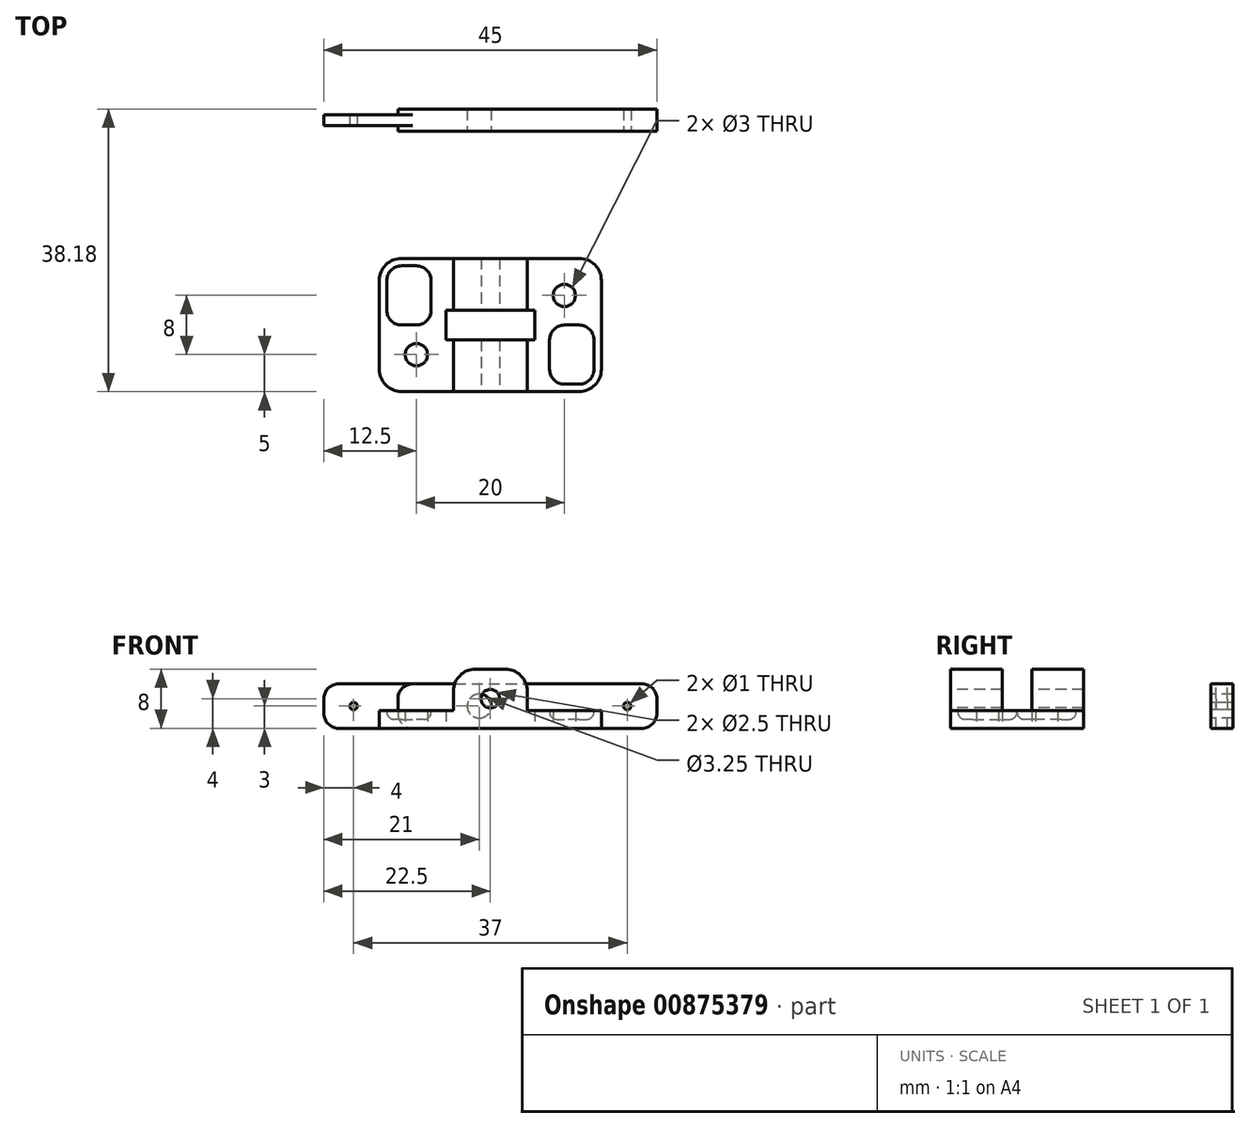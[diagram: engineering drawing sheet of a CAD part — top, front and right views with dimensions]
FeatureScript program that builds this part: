
annotation { "Feature Type Name" : "Feature", "Feature Type Description" : "" }
export const myFeature = defineFeature(function(context is Context, id is Id, definition is map)
    precondition{}
    {
        {
            var Q0;
            Q0=qCreatedBy(makeId("Top.planeOp"),FACE);
            var sketch = newSketch(context, id + "F0", { "sketchPlane" : qUnion([Q0])});
            skLineSegment(sketch, "E0.bottom", {"start": v(15, 9) * mm, "end": v(-15, 9) * mm});
            skLineSegment(sketch, "E0.top", {"start": v(15, -9) * mm, "end": v(-15, -9) * mm});
            skLineSegment(sketch, "E0.left", {"start": v(15, 9) * mm, "end": v(15, -9) * mm});
            skLineSegment(sketch, "E0.right", {"start": v(-15, 9) * mm, "end": v(-15, -9) * mm});
            skPoint(sketch, "E0.middle", {"position": v(0, 0) * mm});
            skLineSegment(sketch, "E1.bottom", {"start": v(6, 2) * mm, "end": v(-6, 2) * mm});
            skLineSegment(sketch, "E1.top", {"start": v(6, -2) * mm, "end": v(-6, -2) * mm});
            skLineSegment(sketch, "E1.left", {"start": v(6, 2) * mm, "end": v(6, -2) * mm});
            skLineSegment(sketch, "E1.right", {"start": v(-6, 2) * mm, "end": v(-6, -2) * mm});
            skLineSegment(sketch, "E2.bottom", {"start": v(15, 9) * mm, "end": v(10, 9) * mm, "construction": true});
            skLineSegment(sketch, "E2.top", {"start": v(15, 4) * mm, "end": v(10, 4) * mm, "construction": true});
            skLineSegment(sketch, "E2.left", {"start": v(15, 9) * mm, "end": v(15, 4) * mm, "construction": true});
            skLineSegment(sketch, "E2.right", {"start": v(10, 9) * mm, "end": v(10, 4) * mm, "construction": true});
            skLineSegment(sketch, "E3.bottom", {"start": v(-15, -9) * mm, "end": v(-10, -9) * mm, "construction": true});
            skLineSegment(sketch, "E3.top", {"start": v(-15, -4) * mm, "end": v(-10, -4) * mm, "construction": true});
            skLineSegment(sketch, "E3.left", {"start": v(-15, -9) * mm, "end": v(-15, -4) * mm, "construction": true});
            skLineSegment(sketch, "E3.right", {"start": v(-10, -9) * mm, "end": v(-10, -4) * mm, "construction": true});
            skCircle(sketch, "E4", {"center": v(-10, -4) * mm, "radius": 1.5 * mm});
            skCircle(sketch, "E5", {"center": v(10, 4) * mm, "radius": 1.5 * mm});
            skLineSegment(sketch, "E6.bottom", {"start": v(-5, 9) * mm, "end": v(5, 9) * mm});
            skLineSegment(sketch, "E6.top", {"start": v(-5, -9) * mm, "end": v(5, -9) * mm});
            skLineSegment(sketch, "E6.left", {"start": v(-5, 9) * mm, "end": v(-5, -9) * mm});
            skLineSegment(sketch, "E6.right", {"start": v(5, 9) * mm, "end": v(5, -9) * mm});
            skLineSegment(sketch, "E7.bottom", {"start": v(-15, 9) * mm, "end": v(-14, 9) * mm, "construction": true});
            skLineSegment(sketch, "E7.top", {"start": v(-15, 8) * mm, "end": v(-14, 8) * mm, "construction": true});
            skLineSegment(sketch, "E7.left", {"start": v(-15, 9) * mm, "end": v(-15, 8) * mm, "construction": true});
            skLineSegment(sketch, "E7.right", {"start": v(-14, 9) * mm, "end": v(-14, 8) * mm, "construction": true});
            skLineSegment(sketch, "E8.bottom", {"start": v(-14, 8) * mm, "end": v(-8, 8) * mm});
            skLineSegment(sketch, "E8.top", {"start": v(-14, 0) * mm, "end": v(-8, 0) * mm});
            skLineSegment(sketch, "E8.left", {"start": v(-14, 8) * mm, "end": v(-14, 0) * mm});
            skLineSegment(sketch, "E8.right", {"start": v(-8, 8) * mm, "end": v(-8, 0) * mm});
            skLineSegment(sketch, "E9.bottom", {"start": v(15, -9) * mm, "end": v(14, -9) * mm, "construction": true});
            skLineSegment(sketch, "E9.top", {"start": v(15, -8) * mm, "end": v(14, -8) * mm, "construction": true});
            skLineSegment(sketch, "E9.left", {"start": v(15, -9) * mm, "end": v(15, -8) * mm, "construction": true});
            skLineSegment(sketch, "E9.right", {"start": v(14, -9) * mm, "end": v(14, -8) * mm, "construction": true});
            skLineSegment(sketch, "E10.bottom", {"start": v(14, -8) * mm, "end": v(8, -8) * mm});
            skLineSegment(sketch, "E10.top", {"start": v(14, 0) * mm, "end": v(8, 0) * mm});
            skLineSegment(sketch, "E10.left", {"start": v(14, -8) * mm, "end": v(14, 0) * mm});
            skLineSegment(sketch, "E10.right", {"start": v(8, -8) * mm, "end": v(8, 0) * mm});
            skSolve(sketch);
        }
        {
            var Q0;
            {var subQ0=sQuery(id+"F0.wireOp",EDGE,"E6.left");var subQ1=sQuery(id+"F0.wireOp",EDGE,"E0.bottom");var subQ2=makeQuery(id+"F0.imprint","INTERSECT",VERTEX,{"derivedFrom":[subQ1,subQ0]});Q0=makeQuery(id+"F0.imprint","IMPRINT",FACE,{"disambiguationData":[TD([[makeQuery(id+"F0.imprint","IMPRINT",EDGE,{"disambiguationData":[TD([[subQ2,1.0]])],"derivedFrom":subQ1}),1.0]])]});}
            var Q1;
            {var subQ6=sQuery(id+"F0.wireOp",EDGE,"E0.right");Q1=makeQuery(id+"F0.imprint","IMPRINT",FACE,{"disambiguationData":[TD([[makeQuery(id+"F0.imprint","IMPRINT",EDGE,{"derivedFrom":subQ6}),1.0]])]});}
            var Q2;
            {var subQ0=sQuery(id+"F0.wireOp",EDGE,"E6.right");var subQ1=sQuery(id+"F0.wireOp",EDGE,"E0.top");var subQ2=makeQuery(id+"F0.imprint","INTERSECT",VERTEX,{"derivedFrom":[subQ1,subQ0]});Q2=makeQuery(id+"F0.imprint","IMPRINT",FACE,{"disambiguationData":[TD([[makeQuery(id+"F0.imprint","IMPRINT",EDGE,{"disambiguationData":[TD([[subQ2,-1.0]])],"derivedFrom":subQ1}),-1.0]])]});}
            var Q3;
            {var subQ10=sQuery(id+"F0.wireOp",EDGE,"E0.left");Q3=makeQuery(id+"F0.imprint","IMPRINT",FACE,{"disambiguationData":[TD([[makeQuery(id+"F0.imprint","IMPRINT",EDGE,{"derivedFrom":subQ10}),-1.0]])]});}
            extrude(context, id + "F1", {"entities" : qUnion([Q0, Q1, Q2, Q3]), "depth" : 2.4 * mm, "offsetDistance" : 25 * mm});
        }
        {
            var Q0;
            {var subQ0=sQuery(id+"F0.wireOp",EDGE,"E6.right");var subQ1=sQuery(id+"F0.wireOp",EDGE,"E0.top");var subQ2=makeQuery(id+"F0.imprint","INTERSECT",VERTEX,{"derivedFrom":[subQ1,subQ0]});Q0=makeQuery(id+"F0.imprint","IMPRINT",FACE,{"disambiguationData":[TD([[makeQuery(id+"F0.imprint","IMPRINT",EDGE,{"disambiguationData":[TD([[subQ2,-1.0]])],"derivedFrom":subQ1}),-1.0]])]});}
            var Q1;
            {var subQ0=sQuery(id+"F0.wireOp",EDGE,"E6.left");var subQ1=sQuery(id+"F0.wireOp",EDGE,"E0.bottom");var subQ2=makeQuery(id+"F0.imprint","INTERSECT",VERTEX,{"derivedFrom":[subQ1,subQ0]});Q1=makeQuery(id+"F0.imprint","IMPRINT",FACE,{"disambiguationData":[TD([[makeQuery(id+"F0.imprint","IMPRINT",EDGE,{"disambiguationData":[TD([[subQ2,1.0]])],"derivedFrom":subQ1}),1.0]])]});}
            extrude(context, id + "F2", {"entities" : qUnion([Q0, Q1]), "operationType" : NewBodyOperationType.ADD, "depth" : 8 * mm, "offsetDistance" : 25 * mm});
        }
        {
            var Q0;
            {var subQ0=sQuery(id+"F0.wireOp",EDGE,"E0.top");Q0=makeQuery(id+"F2.boolean.opBoolean","MERGE",FACE,{"derivedFrom":[makeQuery(id+"F1.opExtrude","SWEPT_FACE",FACE,{"disambiguationData":[OSD([subQ0])]}),makeQuery(id+"F2.opExtrude","SWEPT_FACE",FACE,{"disambiguationData":[OSD([subQ0])]})]});}
            var sketch = newSketch(context, id + "F3", { "sketchPlane" : qUnion([Q0])});
            skLineSegment(sketch, "E11", {"start": v(0, 0) * mm, "end": v(0, 8) * mm, "construction": true});
            skCircle(sketch, "E12", {"center": v(0, 4) * mm, "radius": 1.25 * mm});
            skSolve(sketch);
        }
        {
            var Q0;
            Q0=makeQuery(id+"F3.imprint","IMPRINT",FACE,{"disambiguationData":[TD([[makeQuery(id+"F3.imprint","IMPRINT",EDGE,{"derivedFrom":sQuery(id+"F3.wireOp",EDGE,"E12")}),1.0]])]});
            extrude(context, id + "F4", {"entities" : qUnion([Q0]), "operationType" : NewBodyOperationType.REMOVE, "oppositeDirection" : true, "depth" : 25 * mm, "offsetDistance" : 25 * mm});
        }
        {
            var Q0;
            {var subQ0=sQuery(id+"F0.wireOp",EDGE,"E6.left");Q0=makeQuery(id+"F2.opExtrude","CAP_EDGE",EDGE,{"disambiguationData":[OSD([subQ0]),TDD([makeQuery(id+"F0.imprint","IMPRINT",EDGE,{"disambiguationData":[TD([[makeQuery(id+"F0.imprint","INTERSECT",VERTEX,{"derivedFrom":[sQuery(id+"F0.wireOp",EDGE,"E0.bottom"),subQ0]}),-1.0]])],"derivedFrom":subQ0})])],"isStart":false});}
            var Q1;
            {var subQ0=sQuery(id+"F0.wireOp",EDGE,"E6.right");Q1=makeQuery(id+"F2.opExtrude","CAP_EDGE",EDGE,{"disambiguationData":[OSD([subQ0]),TDD([makeQuery(id+"F0.imprint","IMPRINT",EDGE,{"disambiguationData":[TD([[makeQuery(id+"F0.imprint","INTERSECT",VERTEX,{"derivedFrom":[sQuery(id+"F0.wireOp",EDGE,"E1.bottom"),subQ0]}),1.0]])],"derivedFrom":subQ0})])],"isStart":false});}
            var Q2;
            {var subQ0=sQuery(id+"F0.wireOp",EDGE,"E6.left");Q2=makeQuery(id+"F2.opExtrude","CAP_EDGE",EDGE,{"disambiguationData":[OSD([subQ0]),TDD([makeQuery(id+"F0.imprint","IMPRINT",EDGE,{"disambiguationData":[TD([[makeQuery(id+"F0.imprint","INTERSECT",VERTEX,{"derivedFrom":[sQuery(id+"F0.wireOp",EDGE,"E1.top"),subQ0]}),-1.0]])],"derivedFrom":subQ0})])],"isStart":false});}
            var Q3;
            {var subQ0=sQuery(id+"F0.wireOp",EDGE,"E6.right");Q3=makeQuery(id+"F2.opExtrude","CAP_EDGE",EDGE,{"disambiguationData":[OSD([subQ0]),TDD([makeQuery(id+"F0.imprint","IMPRINT",EDGE,{"disambiguationData":[TD([[makeQuery(id+"F0.imprint","INTERSECT",VERTEX,{"derivedFrom":[sQuery(id+"F0.wireOp",EDGE,"E0.top"),subQ0]}),1.0]])],"derivedFrom":subQ0})])],"isStart":false});}
            var Q4;
            Q4=makeQuery(id+"F1.opExtrude","SWEPT_EDGE",EDGE,{"disambiguationData":[OSD([sQuery(id+"F0.wireOp",EDGE,"E0.top"),sQuery(id+"F0.wireOp",EDGE,"E0.right")])]});
            var Q5;
            Q5=makeQuery(id+"F1.opExtrude","SWEPT_EDGE",EDGE,{"disambiguationData":[OSD([sQuery(id+"F0.wireOp",EDGE,"E0.top"),sQuery(id+"F0.wireOp",EDGE,"E0.left")])]});
            var Q6;
            Q6=makeQuery(id+"F1.opExtrude","SWEPT_EDGE",EDGE,{"disambiguationData":[OSD([sQuery(id+"F0.wireOp",EDGE,"E0.bottom"),sQuery(id+"F0.wireOp",EDGE,"E0.right")])]});
            var Q7;
            Q7=makeQuery(id+"F1.opExtrude","SWEPT_EDGE",EDGE,{"disambiguationData":[OSD([sQuery(id+"F0.wireOp",EDGE,"E0.bottom"),sQuery(id+"F0.wireOp",EDGE,"E0.left")])]});
            fillet(context, id + "F5", {"entities" : qUnion([Q0, Q1, Q2, Q3, Q4, Q5, Q6, Q7]), "radius" : 3 * mm, "tangentPropagation" : true, "allowEdgeOverflow" : false});
        }
        {
            var Q0;
            Q0=makeQuery(id+"F0.imprint","IMPRINT",FACE,{"disambiguationData":[TD([[makeQuery(id+"F0.imprint","IMPRINT",EDGE,{"derivedFrom":sQuery(id+"F0.wireOp",EDGE,"E8.bottom")}),-1.0]])]});
            var Q1;
            Q1=makeQuery(id+"F0.imprint","IMPRINT",FACE,{"disambiguationData":[TD([[makeQuery(id+"F0.imprint","IMPRINT",EDGE,{"derivedFrom":sQuery(id+"F0.wireOp",EDGE,"E10.bottom")}),-1.0]])]});
            extrude(context, id + "F6", {"entities" : qUnion([Q0, Q1]), "operationType" : NewBodyOperationType.ADD, "depth" : 1.2 * mm, "offsetDistance" : 25 * mm});
        }
        {
            var Q0;
            Q0=makeQuery(id+"F1.opExtrude","SWEPT_EDGE",EDGE,{"disambiguationData":[OSD([sQuery(id+"F0.wireOp",EDGE,"E10.bottom"),sQuery(id+"F0.wireOp",EDGE,"E10.left")])]});
            var Q1;
            Q1=makeQuery(id+"F1.opExtrude","SWEPT_EDGE",EDGE,{"disambiguationData":[OSD([sQuery(id+"F0.wireOp",EDGE,"E10.bottom"),sQuery(id+"F0.wireOp",EDGE,"E10.right")])]});
            var Q2;
            Q2=makeQuery(id+"F1.opExtrude","SWEPT_EDGE",EDGE,{"disambiguationData":[OSD([sQuery(id+"F0.wireOp",EDGE,"E10.top"),sQuery(id+"F0.wireOp",EDGE,"E10.left")])]});
            var Q3;
            Q3=makeQuery(id+"F1.opExtrude","SWEPT_EDGE",EDGE,{"disambiguationData":[OSD([sQuery(id+"F0.wireOp",EDGE,"E10.top"),sQuery(id+"F0.wireOp",EDGE,"E10.right")])]});
            var Q4;
            Q4=makeQuery(id+"F1.opExtrude","SWEPT_EDGE",EDGE,{"disambiguationData":[OSD([sQuery(id+"F0.wireOp",EDGE,"E8.bottom"),sQuery(id+"F0.wireOp",EDGE,"E8.right")])]});
            var Q5;
            Q5=makeQuery(id+"F1.opExtrude","SWEPT_EDGE",EDGE,{"disambiguationData":[OSD([sQuery(id+"F0.wireOp",EDGE,"E8.bottom"),sQuery(id+"F0.wireOp",EDGE,"E8.left")])]});
            var Q6;
            Q6=makeQuery(id+"F1.opExtrude","SWEPT_EDGE",EDGE,{"disambiguationData":[OSD([sQuery(id+"F0.wireOp",EDGE,"E8.top"),sQuery(id+"F0.wireOp",EDGE,"E8.right")])]});
            var Q7;
            Q7=makeQuery(id+"F1.opExtrude","SWEPT_EDGE",EDGE,{"disambiguationData":[OSD([sQuery(id+"F0.wireOp",EDGE,"E8.top"),sQuery(id+"F0.wireOp",EDGE,"E8.left")])]});
            fillet(context, id + "F7", {"entities" : qUnion([Q0, Q1, Q2, Q3, Q4, Q5, Q6, Q7]), "radius" : 2 * mm, "tangentPropagation" : true, "allowEdgeOverflow" : false});
        }
        {
            var Q0;
            Q0=makeQuery(id+"F6.opExtrude","CAP_FACE",FACE,{"disambiguationData":[OSD([sQuery(id+"F0.wireOp",EDGE,"E8.bottom"),sQuery(id+"F0.wireOp",EDGE,"E8.top"),sQuery(id+"F0.wireOp",EDGE,"E8.left"),sQuery(id+"F0.wireOp",EDGE,"E8.right")])],"isStart":false});
            var Q1;
            Q1=makeQuery(id+"F6.opExtrude","CAP_FACE",FACE,{"disambiguationData":[OSD([sQuery(id+"F0.wireOp",EDGE,"E10.bottom"),sQuery(id+"F0.wireOp",EDGE,"E10.top"),sQuery(id+"F0.wireOp",EDGE,"E10.left"),sQuery(id+"F0.wireOp",EDGE,"E10.right")])],"isStart":false});
            fillet(context, id + "F8", {"entities" : qUnion([Q0, Q1]), "radius" : 1 * mm, "tangentPropagation" : true, "allowEdgeOverflow" : false});
        }
        {
            var Q0;
            Q0=qCreatedBy(makeId("Top.planeOp"),FACE);
            var sketch = newSketch(context, id + "F9", { "sketchPlane" : qUnion([Q0])});
            skLineSegment(sketch, "E13.bottom", {"start": v(-22.5, 26.18) * mm, "end": v(22.5, 26.18) * mm});
            skLineSegment(sketch, "E13.top", {"start": v(-22.5, 29.18) * mm, "end": v(22.5, 29.18) * mm});
            skLineSegment(sketch, "E13.left", {"start": v(-22.5, 26.18) * mm, "end": v(-22.5, 29.18) * mm});
            skLineSegment(sketch, "E13.right", {"start": v(22.5, 26.18) * mm, "end": v(22.5, 29.18) * mm});
            skPoint(sketch, "E13.middle", {"position": v(0, 27.68) * mm});
            skLineSegment(sketch, "E14.bottom", {"start": v(-22.5, 26.18) * mm, "end": v(-12.5, 26.18) * mm});
            skLineSegment(sketch, "E14.top", {"start": v(-22.5, 26.93) * mm, "end": v(-12.5, 26.93) * mm});
            skLineSegment(sketch, "E14.left", {"start": v(-22.5, 26.18) * mm, "end": v(-22.5, 26.93) * mm});
            skLineSegment(sketch, "E14.right", {"start": v(-12.5, 26.18) * mm, "end": v(-12.5, 26.93) * mm});
            skLineSegment(sketch, "E15.bottom", {"start": v(-22.5, 29.18) * mm, "end": v(-12.5, 29.18) * mm});
            skLineSegment(sketch, "E15.top", {"start": v(-22.5, 28.43) * mm, "end": v(-12.5, 28.43) * mm});
            skLineSegment(sketch, "E15.left", {"start": v(-22.5, 29.18) * mm, "end": v(-22.5, 28.43) * mm});
            skLineSegment(sketch, "E15.right", {"start": v(-12.5, 29.18) * mm, "end": v(-12.5, 28.43) * mm});
            skSolve(sketch);
        }
        {
            var Q0;
            {var subQ3=sQuery(id+"F9.wireOp",EDGE,"E13.right");Q0=makeQuery(id+"F9.imprint","IMPRINT",FACE,{"disambiguationData":[TD([[makeQuery(id+"F9.imprint","IMPRINT",EDGE,{"derivedFrom":subQ3}),1.0]])]});}
            extrude(context, id + "F10", {"entities" : qUnion([Q0]), "depth" : 6 * mm, "offsetDistance" : 25 * mm});
        }
        {
            var Q0;
            Q0=makeQuery(id+"F10.opExtrude","SWEPT_FACE",FACE,{"disambiguationData":[OSD([sQuery(id+"F9.wireOp",EDGE,"E14.top")])]});
            var sketch = newSketch(context, id + "F11", { "sketchPlane" : qUnion([Q0])});
            skLineSegment(sketch, "E16", {"start": v(-22.5, 3) * mm, "end": v(-18.5, 3) * mm, "construction": true});
            skCircle(sketch, "E17", {"center": v(-18.5, 3) * mm, "radius": 0.5 * mm});
            skSolve(sketch);
        }
        {
            var Q0;
            Q0=makeQuery(id+"F11.imprint","IMPRINT",FACE,{"disambiguationData":[TD([[makeQuery(id+"F11.imprint","IMPRINT",EDGE,{"derivedFrom":sQuery(id+"F11.wireOp",EDGE,"E17")}),1.0]])]});
            extrude(context, id + "F12", {"entities" : qUnion([Q0]), "operationType" : NewBodyOperationType.REMOVE, "oppositeDirection" : true, "depth" : 25 * mm, "offsetDistance" : 25 * mm});
        }
        {
            var Q0;
            Q0=makeQuery(id+"F10.opExtrude","SWEPT_FACE",FACE,{"disambiguationData":[OSD([sQuery(id+"F9.wireOp",EDGE,"E13.bottom")])]});
            var sketch = newSketch(context, id + "F13", { "sketchPlane" : qUnion([Q0])});
            skLineSegment(sketch, "E18", {"start": v(22.5, 3) * mm, "end": v(18.5, 3) * mm, "construction": true});
            skLineSegment(sketch, "E19", {"start": v(18.5, 3) * mm, "end": v(-1.5, 3) * mm, "construction": true});
            skCircle(sketch, "E20", {"center": v(18.5, 3) * mm, "radius": 0.5 * mm});
            skCircle(sketch, "E21", {"center": v(-1.5, 3) * mm, "radius": 1.63 * mm});
            skSolve(sketch);
        }
        {
            var Q0;
            Q0=makeQuery(id+"F13.imprint","IMPRINT",FACE,{"disambiguationData":[TD([[makeQuery(id+"F13.imprint","IMPRINT",EDGE,{"derivedFrom":sQuery(id+"F13.wireOp",EDGE,"E21")}),1.0]])]});
            var Q1;
            Q1=makeQuery(id+"F13.imprint","IMPRINT",FACE,{"disambiguationData":[TD([[makeQuery(id+"F13.imprint","IMPRINT",EDGE,{"derivedFrom":sQuery(id+"F13.wireOp",EDGE,"E20")}),1.0]])]});
            extrude(context, id + "F14", {"entities" : qUnion([Q0, Q1]), "operationType" : NewBodyOperationType.REMOVE, "oppositeDirection" : true, "depth" : 25 * mm, "offsetDistance" : 25 * mm});
        }
        {
            var Q0;
            Q0=makeQuery(id+"F10.opExtrude","CAP_EDGE",EDGE,{"disambiguationData":[OSD([sQuery(id+"F9.wireOp",EDGE,"E13.left")])],"isStart":false});
            var Q1;
            Q1=makeQuery(id+"F10.opExtrude","CAP_EDGE",EDGE,{"disambiguationData":[OSD([sQuery(id+"F9.wireOp",EDGE,"E13.left")])],"isStart":true});
            var Q2;
            Q2=makeQuery(id+"F10.opExtrude","CAP_EDGE",EDGE,{"disambiguationData":[OSD([sQuery(id+"F9.wireOp",EDGE,"E13.right")])],"isStart":false});
            var Q3;
            Q3=makeQuery(id+"F10.opExtrude","CAP_EDGE",EDGE,{"disambiguationData":[OSD([sQuery(id+"F9.wireOp",EDGE,"E13.right")])],"isStart":true});
            var Q4;
            Q4=makeQuery(id+"F10.opExtrude","CAP_EDGE",EDGE,{"disambiguationData":[OSD([sQuery(id+"F9.wireOp",EDGE,"E14.right")])],"isStart":true});
            var Q5;
            Q5=makeQuery(id+"F10.opExtrude","CAP_EDGE",EDGE,{"disambiguationData":[OSD([sQuery(id+"F9.wireOp",EDGE,"E15.right")])],"isStart":true});
            var Q6;
            Q6=makeQuery(id+"F10.opExtrude","CAP_EDGE",EDGE,{"disambiguationData":[OSD([sQuery(id+"F9.wireOp",EDGE,"E14.right")])],"isStart":false});
            var Q7;
            Q7=makeQuery(id+"F10.opExtrude","CAP_EDGE",EDGE,{"disambiguationData":[OSD([sQuery(id+"F9.wireOp",EDGE,"E15.right")])],"isStart":false});
            fillet(context, id + "F15", {"entities" : qUnion([Q0, Q1, Q2, Q3, Q4, Q5, Q6, Q7]), "radius" : 2 * mm, "tangentPropagation" : true, "allowEdgeOverflow" : false});
        }
    });
